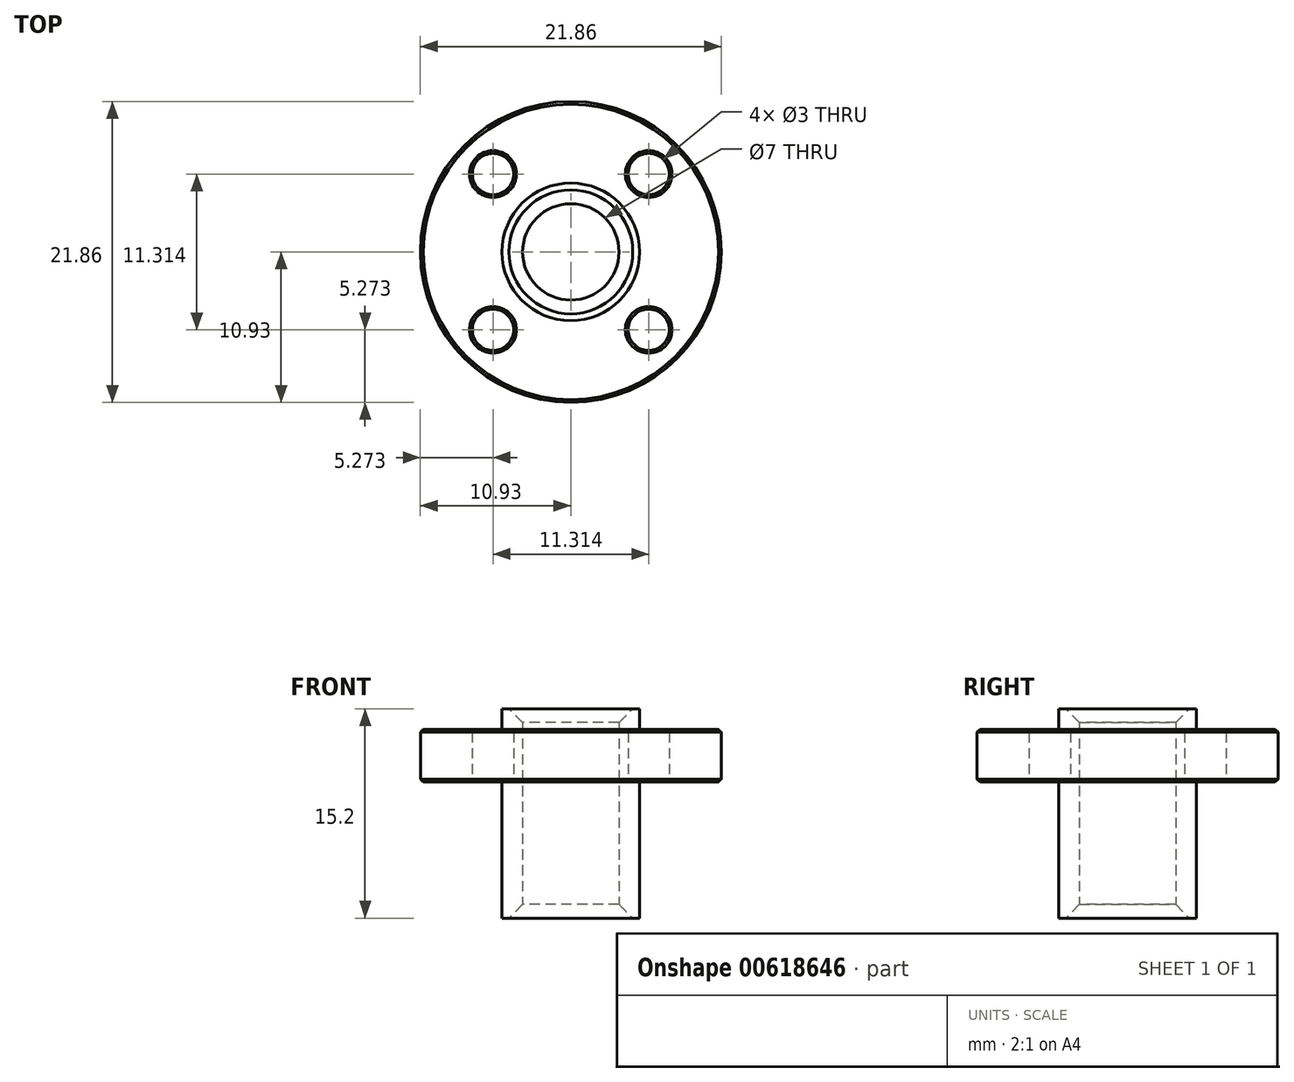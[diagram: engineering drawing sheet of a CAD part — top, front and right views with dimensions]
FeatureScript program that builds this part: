
annotation { "Feature Type Name" : "Feature", "Feature Type Description" : "" }
export const myFeature = defineFeature(function(context is Context, id is Id, definition is map)
    precondition{}
    {
        {
            var Q0;
            Q0=qCreatedBy(makeId("Top.planeOp"),FACE);
            var sketch = newSketch(context, id + "F0", { "sketchPlane" : qUnion([Q0])});
            skCircle(sketch, "E0", {"center": v(0, 0) * mm, "radius": 10.93 * mm});
            skCircle(sketch, "E1", {"center": v(0, 0) * mm, "radius": 3.5 * mm});
            skCircle(sketch, "E2", {"center": v(5.66, -5.66) * mm, "radius": 1.5 * mm});
            skCircle(sketch, "E3", {"center": v(5.66, 5.66) * mm, "radius": 1.5 * mm});
            skCircle(sketch, "E4", {"center": v(-5.66, 5.66) * mm, "radius": 1.5 * mm});
            skCircle(sketch, "E5", {"center": v(-5.66, -5.66) * mm, "radius": 1.5 * mm});
            skLineSegment(sketch, "E6.trimOffspring", {"start": v(5.66, 5.66) * mm, "end": v(0, 0) * mm, "construction": true});
            skLineSegment(sketch, "E7.trimOffspring", {"start": v(-5.66, 5.66) * mm, "end": v(0, 0) * mm, "construction": true});
            skLineSegment(sketch, "E8.trimOffspring", {"start": v(0, 0) * mm, "end": v(5.66, -5.66) * mm, "construction": true});
            skLineSegment(sketch, "E9.trimOffspring", {"start": v(0, 0) * mm, "end": v(-5.66, -5.66) * mm, "construction": true});
            skCircle(sketch, "E10", {"center": v(0, 0) * mm, "radius": 5 * mm});
            skLineSegment(sketch, "E11.0", {"start": v(0, 0) * mm, "end": v(0, 0) * mm});
            skLineSegment(sketch, "E11.1", {"start": v(0, 0) * mm, "end": v(5.66, 5.66) * mm, "construction": true});
            skSolve(sketch);
        }
        {
            var Q0;
            Q0 = qSketchRegion(id + "F0", true);
            extrude(context, id + "F1", {"entities" : qUnion([Q0]), "depth" : 3.8 * mm, "offsetDistance" : 25 * mm});
        }
        {
            var Q0;
            Q0=makeQuery(id+"F0.imprint","IMPRINT",FACE,{"disambiguationData":[TD([[makeQuery(id+"F0.imprint","IMPRINT",EDGE,{"derivedFrom":sQuery(id+"F0.wireOp",EDGE,"E1")}),-1.0]])]});
            extrude(context, id + "F2", {"entities" : qUnion([Q0]), "operationType" : NewBodyOperationType.ADD, "depth" : 5.3 * mm, "offsetDistance" : 25 * mm});
        }
        {
            var Q0;
            Q0=makeQuery(id+"F0.imprint","IMPRINT",FACE,{"disambiguationData":[TD([[makeQuery(id+"F0.imprint","IMPRINT",EDGE,{"derivedFrom":sQuery(id+"F0.wireOp",EDGE,"E1")}),-1.0]])]});
            extrude(context, id + "F3", {"entities" : qUnion([Q0]), "operationType" : NewBodyOperationType.ADD, "oppositeDirection" : true, "depth" : 9.9 * mm, "offsetDistance" : 25 * mm});
        }
        {
            var Q0;
            Q0=makeQuery(id+"F2.opExtrude","CAP_EDGE",EDGE,{"disambiguationData":[OSD([sQuery(id+"F0.wireOp",EDGE,"E1")])],"isStart":false});
            var Q1;
            Q1=makeQuery(id+"F3.opExtrude","CAP_EDGE",EDGE,{"disambiguationData":[OSD([sQuery(id+"F0.wireOp",EDGE,"E1")])],"isStart":false});
            chamfer(context, id + "F4", {"entities" : qUnion([Q0, Q1]), "width" : 1 * mm, "tangentPropagation" : true});
        }
        {
            var Q0;
            Q0=makeQuery(id+"F1.opExtrude","CAP_EDGE",EDGE,{"disambiguationData":[OSD([sQuery(id+"F0.wireOp",EDGE,"E4")])],"isStart":false});
            var Q1;
            Q1=makeQuery(id+"F1.opExtrude","CAP_EDGE",EDGE,{"disambiguationData":[OSD([sQuery(id+"F0.wireOp",EDGE,"E5")])],"isStart":false});
            var Q2;
            Q2=makeQuery(id+"F1.opExtrude","CAP_EDGE",EDGE,{"disambiguationData":[OSD([sQuery(id+"F0.wireOp",EDGE,"E2")])],"isStart":false});
            var Q3;
            Q3=makeQuery(id+"F1.opExtrude","CAP_EDGE",EDGE,{"disambiguationData":[OSD([sQuery(id+"F0.wireOp",EDGE,"E3")])],"isStart":false});
            var Q4;
            Q4=makeQuery(id+"F1.opExtrude","CAP_EDGE",EDGE,{"disambiguationData":[OSD([sQuery(id+"F0.wireOp",EDGE,"E0")])],"isStart":false});
            var Q5;
            Q5=makeQuery(id+"F1.opExtrude","CAP_EDGE",EDGE,{"disambiguationData":[OSD([sQuery(id+"F0.wireOp",EDGE,"E0")])],"isStart":true});
            chamfer(context, id + "F5", {"entities" : qUnion([Q0, Q1, Q2, Q3, Q4, Q5]), "width" : 0.2 * mm, "tangentPropagation" : true});
        }
    });
